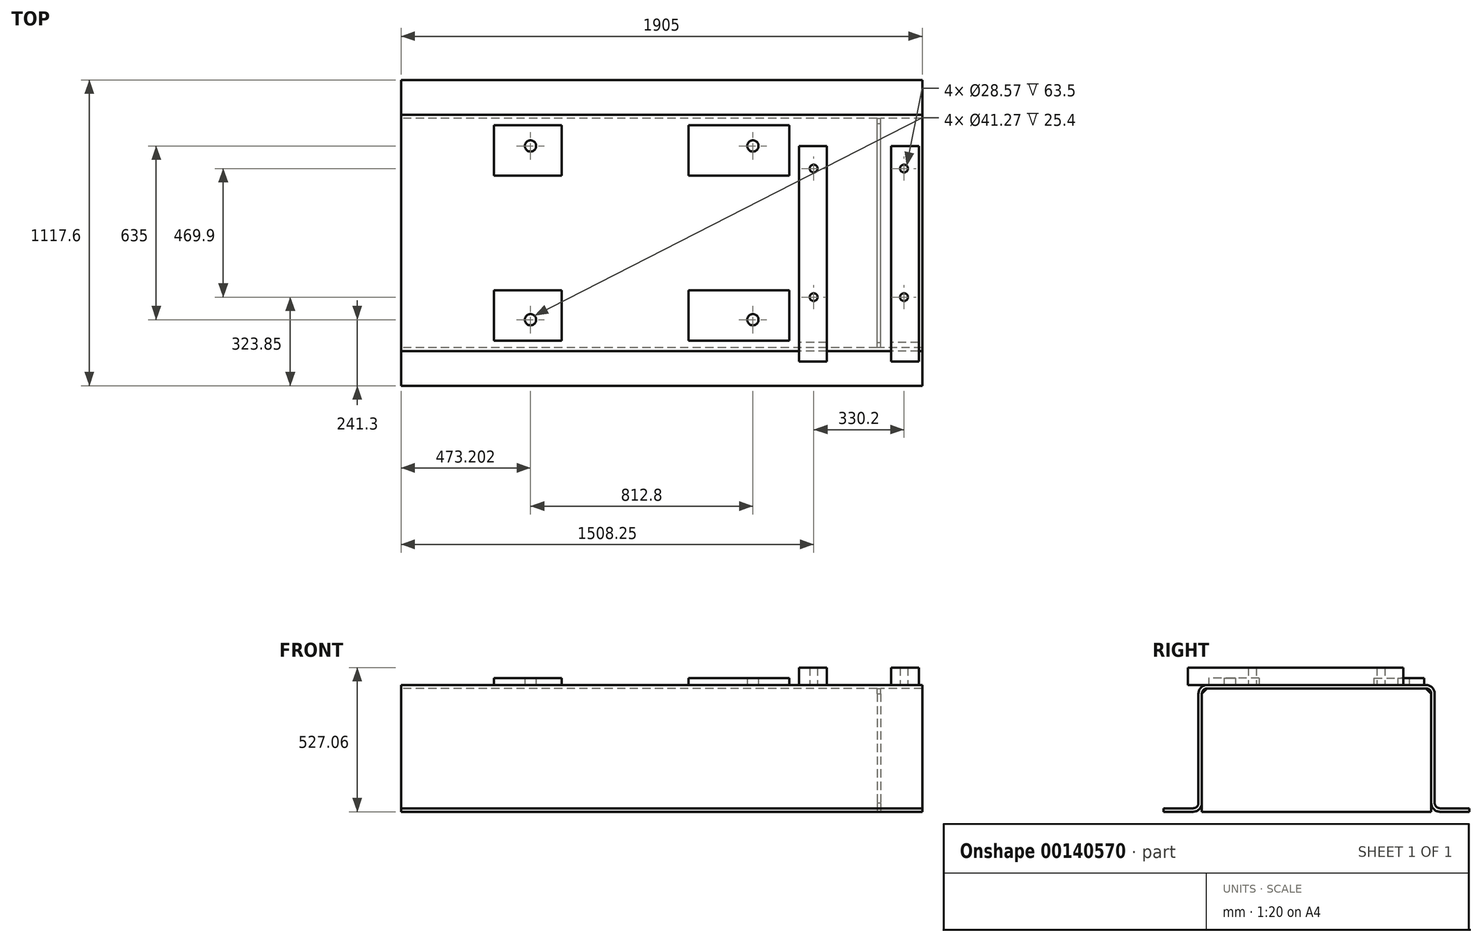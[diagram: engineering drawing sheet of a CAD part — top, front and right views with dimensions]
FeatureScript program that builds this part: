
annotation { "Feature Type Name" : "Feature", "Feature Type Description" : "" }
export const myFeature = defineFeature(function(context is Context, id is Id, definition is map)
    precondition{}
    {
        {
            var Q0;
            Q0=qCreatedBy(makeId("Right.planeOp"),FACE);
            var sketch = newSketch(context, id + "F0", { "sketchPlane" : qUnion([Q0])});
            skLineSegment(sketch, "E0.rect.bottom", {"start": v(-400.05, 231.78) * mm, "end": v(400.05, 231.78) * mm});
            skLineSegment(sketch, "E0.rect.top", {"start": v(-558.8, -231.78) * mm, "end": v(-450.85, -231.78) * mm});
            skLineSegment(sketch, "E0.rect.left", {"start": v(-431.8, 200.03) * mm, "end": v(-431.8, -200.03) * mm});
            skLineSegment(sketch, "E0.rect.right", {"start": v(431.8, 200.03) * mm, "end": v(431.8, -200.03) * mm});
            skPoint(sketch, "E0.rect.middle", {"position": v(0, 0) * mm});
            skLineSegment(sketch, "E1.0", {"start": v(-400.05, 219.08) * mm, "end": v(400.05, 219.08) * mm});
            skLineSegment(sketch, "E1.1", {"start": v(-419.1, 200.03) * mm, "end": v(-419.1, -200.03) * mm});
            skLineSegment(sketch, "E1.2", {"start": v(-558.8, -219.08) * mm, "end": v(-450.85, -219.08) * mm});
            skLineSegment(sketch, "E1.3", {"start": v(419.1, 200.03) * mm, "end": v(419.1, -200.03) * mm});
            skLineSegment(sketch, "E2.0", {"start": v(-558.8, -219.08) * mm, "end": v(-558.8, -231.78) * mm});
            skLineSegment(sketch, "E3", {"start": v(0, 0) * mm, "end": v(0, 438.25) * mm, "construction": true});
            skPoint(sketch, "E4.orphan", {"position": v(-431.8, -231.78) * mm});
            skLineSegment(sketch, "E5.MirrorCS", {"start": v(558.8, -219.08) * mm, "end": v(558.8, -231.78) * mm});
            skLineSegment(sketch, "E6.MirrorCS", {"start": v(558.8, -219.08) * mm, "end": v(450.85, -219.08) * mm});
            skLineSegment(sketch, "E7.MirrorCS", {"start": v(558.8, -231.78) * mm, "end": v(450.85, -231.78) * mm});
            skPoint(sketch, "E8.MirrorP", {"position": v(431.8, -231.78) * mm});
            skPoint(sketch, "E9.visualSharp", {"position": v(-431.8, -219.08) * mm});
            skArc(sketch, "E9.filletArc", {"start": v(-450.85, -219.08) * mm, "mid": v(-437.38, -213.5) * mm, "end": v(-431.8, -200.03) * mm});
            skPoint(sketch, "E10.visualSharp", {"position": v(-419.1, 219.08) * mm});
            skArc(sketch, "E10.filletArc", {"start": v(-400.05, 219.08) * mm, "mid": v(-413.52, 213.5) * mm, "end": v(-419.1, 200.03) * mm});
            skPoint(sketch, "E11.visualSharp", {"position": v(419.1, 219.08) * mm});
            skArc(sketch, "E11.filletArc", {"start": v(419.1, 200.03) * mm, "mid": v(413.52, 213.5) * mm, "end": v(400.05, 219.08) * mm});
            skPoint(sketch, "E12.visualSharp", {"position": v(431.8, -219.08) * mm});
            skArc(sketch, "E12.filletArc", {"start": v(431.8, -200.03) * mm, "mid": v(437.38, -213.5) * mm, "end": v(450.85, -219.08) * mm});
            skPoint(sketch, "E13.visualSharp", {"position": v(-419.1, -231.78) * mm});
            skArc(sketch, "E13.filletArc", {"start": v(-450.85, -231.78) * mm, "mid": v(-428.4, -222.48) * mm, "end": v(-419.1, -200.03) * mm});
            skPoint(sketch, "E14.visualSharp", {"position": v(-431.8, 231.78) * mm});
            skArc(sketch, "E14.filletArc", {"start": v(-400.05, 231.78) * mm, "mid": v(-422.5, 222.48) * mm, "end": v(-431.8, 200.03) * mm});
            skPoint(sketch, "E15.visualSharp", {"position": v(431.8, 231.78) * mm});
            skArc(sketch, "E15.filletArc", {"start": v(431.8, 200.03) * mm, "mid": v(422.5, 222.48) * mm, "end": v(400.05, 231.78) * mm});
            skPoint(sketch, "E16.visualSharp", {"position": v(419.1, -231.78) * mm});
            skArc(sketch, "E16.filletArc", {"start": v(419.1, -200.03) * mm, "mid": v(428.4, -222.48) * mm, "end": v(450.85, -231.78) * mm});
            skSolve(sketch);
        }
        {
            var Q0;
            Q0=qSketchRegion(id+"F0",true);
            extrude(context, id + "F1", {"entities" : qUnion([Q0]), "endBound" : BoundingType.SYMMETRIC, "depth" : 1905 * mm});
        }
        {
            var Q0;
            Q0=makeQuery(id+"F1.opExtrude","SWEPT_FACE",FACE,{"disambiguationData":[OSD([sQuery(id+"F0.wireOp",EDGE,"E0.rect.bottom")])]});
            var sketch = newSketch(context, id + "F2", { "sketchPlane" : qUnion([Q0])});
            skLineSegment(sketch, "E17", {"start": v(-1090.5, 0) * mm, "end": v(1245.35, 0) * mm, "construction": true});
            skLineSegment(sketch, "E18.0", {"start": v(-952.5, -400.05) * mm, "end": v(-952.5, 400.05) * mm, "construction": true});
            skLineSegment(sketch, "E19.0", {"start": v(-72.9, -400.05) * mm, "end": v(-72.9, 400.05) * mm, "construction": true});
            skLineSegment(sketch, "E20.0", {"start": v(720.85, -400.05) * mm, "end": v(720.85, 400.05) * mm, "construction": true});
            skLineSegment(sketch, "E21.0", {"start": v(838.2, -469.9) * mm, "end": v(838.2, 317.5) * mm});
            skLineSegment(sketch, "E22.0", {"start": v(939.8, -469.9) * mm, "end": v(939.8, 317.5) * mm});
            skLineSegment(sketch, "E23.0", {"start": v(-1090.5, 317.5) * mm, "end": v(-72.9, 317.5) * mm});
            skLineSegment(sketch, "E24.0", {"start": v(838.2, -469.9) * mm, "end": v(939.8, -469.9) * mm});
            skLineSegment(sketch, "E25.trimOffspring", {"start": v(838.2, 317.5) * mm, "end": v(939.8, 317.5) * mm});
            skLineSegment(sketch, "E26.0", {"start": v(885.95, -400.05) * mm, "end": v(885.95, 400.05) * mm, "construction": true});
            skLineSegment(sketch, "E27.0", {"start": v(-1090.5, 234.95) * mm, "end": v(1245.35, 234.95) * mm, "construction": true});
            skLineSegment(sketch, "E28.0", {"start": v(-1090.5, -234.95) * mm, "end": v(1245.35, -234.95) * mm, "construction": true});
            skCircle(sketch, "E29", {"center": v(885.95, 234.95) * mm, "radius": 14.29 * mm});
            skCircle(sketch, "E30.MirrorC", {"center": v(885.95, -234.95) * mm, "radius": 14.29 * mm});
            skCircle(sketch, "E31.MirrorC", {"center": v(555.75, -234.95) * mm, "radius": 14.29 * mm});
            skCircle(sketch, "E32.MirrorC", {"center": v(555.75, 234.95) * mm, "radius": 14.29 * mm});
            skLineSegment(sketch, "E33.MirrorCS", {"start": v(603.5, -469.9) * mm, "end": v(501.9, -469.9) * mm});
            skLineSegment(sketch, "E34.MirrorCS", {"start": v(603.5, 317.5) * mm, "end": v(501.9, 317.5) * mm});
            skLineSegment(sketch, "E35.MirrorCS", {"start": v(603.5, -469.9) * mm, "end": v(603.5, 317.5) * mm});
            skLineSegment(sketch, "E36.MirrorCS", {"start": v(501.9, -469.9) * mm, "end": v(501.9, 317.5) * mm});
            skSolve(sketch);
        }
        {
            var Q0;
            Q0=qSketchRegion(id+"F2",true);
            extrude(context, id + "F3", {"entities" : qUnion([Q0]), "operationType" : NewBodyOperationType.ADD, "depth" : 63.5 * mm});
        }
        {
            var Q0;
            {var subQ6=sQuery(id+"F2.wireOp",EDGE,"E25.trimOffspring");Q0=makeQuery(id+"F2.imprint","IMPRINT",FACE,{"disambiguationData":[TD([[makeQuery(id+"F2.imprint","IMPRINT",EDGE,{"derivedFrom":subQ6}),1.0]])]});}
            var sketch = newSketch(context, id + "F4", { "sketchPlane" : qUnion([Q0])});
            skLineSegment(sketch, "E37.0", {"start": v(98.55, -400.05) * mm, "end": v(98.55, 400.05) * mm, "construction": true});
            skLineSegment(sketch, "E38.0", {"start": v(466.85, -400.05) * mm, "end": v(466.85, 400.05) * mm, "construction": true});
            skLineSegment(sketch, "E39.0", {"start": v(-365, -400.05) * mm, "end": v(-365, 400.05) * mm, "construction": true});
            skLineSegment(sketch, "E40.0", {"start": v(-612.65, -400.05) * mm, "end": v(-612.65, 400.05) * mm, "construction": true});
            skLineSegment(sketch, "E41.0", {"start": v(-1090.5, -209.55) * mm, "end": v(1245.35, -209.55) * mm, "construction": true});
            skLineSegment(sketch, "E42.0", {"start": v(-1090.5, -393.7) * mm, "end": v(1245.35, -393.7) * mm, "construction": true});
            skLineSegment(sketch, "E43.bottom", {"start": v(466.85, -209.55) * mm, "end": v(98.55, -209.55) * mm});
            skLineSegment(sketch, "E43.top", {"start": v(466.85, -393.7) * mm, "end": v(98.55, -393.7) * mm});
            skLineSegment(sketch, "E43.left", {"start": v(466.85, -209.55) * mm, "end": v(466.85, -393.7) * mm});
            skLineSegment(sketch, "E43.right", {"start": v(98.55, -209.55) * mm, "end": v(98.55, -393.7) * mm});
            skLineSegment(sketch, "E44.bottom", {"start": v(-365, -209.55) * mm, "end": v(-612.65, -209.55) * mm});
            skLineSegment(sketch, "E44.top", {"start": v(-365, -393.7) * mm, "end": v(-612.65, -393.7) * mm});
            skLineSegment(sketch, "E44.left", {"start": v(-365, -209.55) * mm, "end": v(-365, -393.7) * mm});
            skLineSegment(sketch, "E44.right", {"start": v(-612.65, -209.55) * mm, "end": v(-612.65, -393.7) * mm});
            skLineSegment(sketch, "E45.0", {"start": v(333.5, -400.05) * mm, "end": v(333.5, 400.05) * mm, "construction": true});
            skLineSegment(sketch, "E46.0", {"start": v(-479.3, -400.05) * mm, "end": v(-479.3, 400.05) * mm, "construction": true});
            skLineSegment(sketch, "E47.0", {"start": v(-1090.5, -317.5) * mm, "end": v(1245.35, -317.5) * mm, "construction": true});
            skCircle(sketch, "E48", {"center": v(-479.3, -317.5) * mm, "radius": 20.64 * mm});
            skCircle(sketch, "E49", {"center": v(333.5, -317.5) * mm, "radius": 20.64 * mm});
            skCircle(sketch, "E50.MirrorC", {"center": v(333.5, 317.5) * mm, "radius": 20.64 * mm});
            skCircle(sketch, "E51.MirrorC", {"center": v(-479.3, 317.5) * mm, "radius": 20.64 * mm});
            skLineSegment(sketch, "E52.MirrorCS", {"start": v(-612.65, 209.55) * mm, "end": v(-612.65, 393.7) * mm});
            skLineSegment(sketch, "E53.MirrorCS", {"start": v(-365, 209.55) * mm, "end": v(-365, 393.7) * mm});
            skLineSegment(sketch, "E54.MirrorCS", {"start": v(-365, 393.7) * mm, "end": v(-612.65, 393.7) * mm});
            skLineSegment(sketch, "E55.MirrorCS", {"start": v(466.85, 209.55) * mm, "end": v(98.55, 209.55) * mm});
            skLineSegment(sketch, "E56.MirrorCS", {"start": v(466.85, 393.7) * mm, "end": v(98.55, 393.7) * mm});
            skLineSegment(sketch, "E57.MirrorCS", {"start": v(466.85, 209.55) * mm, "end": v(466.85, 393.7) * mm});
            skLineSegment(sketch, "E58.MirrorCS", {"start": v(98.55, 209.55) * mm, "end": v(98.55, 393.7) * mm});
            skLineSegment(sketch, "E59.MirrorCS", {"start": v(-365, 209.55) * mm, "end": v(-612.65, 209.55) * mm});
            skSolve(sketch);
        }
        {
            var Q0;
            Q0=qSketchRegion(id+"F4",true);
            extrude(context, id + "F5", {"entities" : qUnion([Q0]), "operationType" : NewBodyOperationType.ADD, "depth" : 25.4 * mm});
        }
        {
            var Q0;
            Q0=makeQuery(id+"F1.opExtrude","CAP_FACE",FACE,{"disambiguationData":[OSD([sQuery(id+"F0.wireOp",EDGE,"E0.rect.bottom"),sQuery(id+"F0.wireOp",EDGE,"E0.rect.top"),sQuery(id+"F0.wireOp",EDGE,"E0.rect.left"),sQuery(id+"F0.wireOp",EDGE,"E0.rect.right"),sQuery(id+"F0.wireOp",EDGE,"E1.0"),sQuery(id+"F0.wireOp",EDGE,"E1.1"),sQuery(id+"F0.wireOp",EDGE,"E1.2"),sQuery(id+"F0.wireOp",EDGE,"E1.3"),sQuery(id+"F0.wireOp",EDGE,"E2.0"),sQuery(id+"F0.wireOp",EDGE,"E5.MirrorCS"),sQuery(id+"F0.wireOp",EDGE,"E6.MirrorCS"),sQuery(id+"F0.wireOp",EDGE,"E7.MirrorCS"),sQuery(id+"F0.wireOp",EDGE,"E9.filletArc"),sQuery(id+"F0.wireOp",EDGE,"E10.filletArc"),sQuery(id+"F0.wireOp",EDGE,"E11.filletArc"),sQuery(id+"F0.wireOp",EDGE,"E12.filletArc"),sQuery(id+"F0.wireOp",EDGE,"E13.filletArc"),sQuery(id+"F0.wireOp",EDGE,"E14.filletArc"),sQuery(id+"F0.wireOp",EDGE,"E15.filletArc"),sQuery(id+"F0.wireOp",EDGE,"E16.filletArc")])],"isStart":false});
            cPlane(context, id + "F6", {"entities" : qUnion([Q0]), "cplaneType" : CPlaneType.OFFSET, "offset" : 152.4 * mm, "oppositeDirection" : true, "width" : 152.4 * mm, "height" : 152.4 * mm});
        }
        {
            var Q0;
            Q0=qCreatedBy(id+"F6.planeOp",FACE);
            var sketch = newSketch(context, id + "F7", { "sketchPlane" : qUnion([Q0])});
            skLineSegment(sketch, "E60.0", {"start": v(-400.05, 219.08) * mm, "end": v(400.05, 219.08) * mm});
            skLineSegment(sketch, "E61.0", {"start": v(-419.1, 200.03) * mm, "end": v(-419.1, -231.78) * mm});
            skLineSegment(sketch, "E62.0", {"start": v(419.1, 200.03) * mm, "end": v(419.1, -231.78) * mm});
            skLineSegment(sketch, "E63.0", {"start": v(-558.8, -231.78) * mm, "end": v(419.1, -231.78) * mm});
            skLineSegment(sketch, "E64", {"start": v(-419.1, 200.03) * mm, "end": v(-400.05, 219.08) * mm});
            skLineSegment(sketch, "E65", {"start": v(400.05, 219.08) * mm, "end": v(419.1, 200.03) * mm});
            skPoint(sketch, "E66.orphan", {"position": v(-450.85, -231.78) * mm});
            skPoint(sketch, "E67.orphan", {"position": v(419.1, -200.03) * mm});
            skPoint(sketch, "E68.orphan", {"position": v(-419.1, -200.03) * mm});
            skSolve(sketch);
        }
        {
            var Q0;
            Q0=qSketchRegion(id+"F7",true);
            extrude(context, id + "F8", {"entities" : qUnion([Q0]), "operationType" : NewBodyOperationType.ADD, "oppositeDirection" : true, "depth" : 12.7 * mm});
        }
    });
